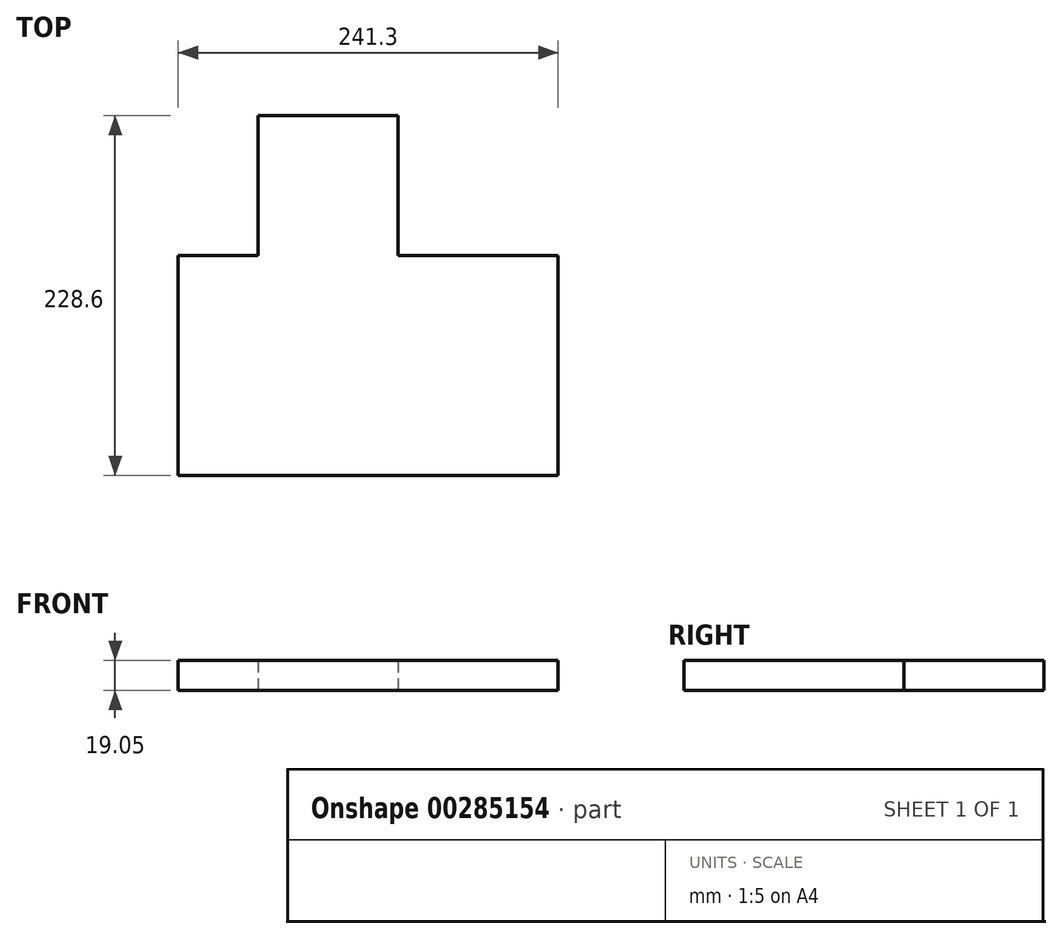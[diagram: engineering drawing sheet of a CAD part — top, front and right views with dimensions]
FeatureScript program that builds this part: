
annotation { "Feature Type Name" : "Feature", "Feature Type Description" : "" }
export const myFeature = defineFeature(function(context is Context, id is Id, definition is map)
    precondition{}
    {
        {
            var Q0;
            Q0=qCreatedBy(makeId("Top.planeOp"),FACE);
            var sketch = newSketch(context, id + "F0", { "sketchPlane" : qUnion([Q0])});
            skLineSegment(sketch, "E0", {"start": v(-46.63, 84.13) * mm, "end": v(-46.63, 173.03) * mm});
            skLineSegment(sketch, "E1", {"start": v(-46.63, 173.03) * mm, "end": v(42.27, 173.03) * mm});
            skLineSegment(sketch, "E2", {"start": v(42.27, 173.03) * mm, "end": v(42.27, 84.13) * mm});
            skLineSegment(sketch, "E3", {"start": v(42.27, 84.13) * mm, "end": v(143.87, 84.13) * mm});
            skLineSegment(sketch, "E4", {"start": v(143.87, 84.13) * mm, "end": v(143.87, -55.57) * mm});
            skLineSegment(sketch, "E5", {"start": v(143.87, -55.57) * mm, "end": v(-97.43, -55.57) * mm});
            skLineSegment(sketch, "E6", {"start": v(-97.43, -55.57) * mm, "end": v(-97.43, 84.13) * mm});
            skLineSegment(sketch, "E7", {"start": v(-97.43, 84.13) * mm, "end": v(-46.63, 84.13) * mm});
            skSolve(sketch);
        }
        {
            var Q0;
            Q0=makeQuery(id+"F0.imprint","IMPRINT",FACE,{"disambiguationData":[TD([[makeQuery(id+"F0.imprint","IMPRINT",EDGE,{"derivedFrom":sQuery(id+"F0.wireOp",EDGE,"E0")}),-1.0]])]});
            extrude(context, id + "F1", {"entities" : qUnion([Q0]), "depth" : 19.05 * mm});
        }
    });
